# Revit family: 306_H7_W_-S7
name_source: partatom
category: Pipe Accessories
units: mm (PartAtom-declared; Revit-internal decimal feet)

## family parameters
Always vertical = Yes
Cut with Voids When Loaded = No
Part Type = Valve - Breaks Into
Round Connector Dimension = Use Diameter
Shared = No
Work Plane-Based = No

## types (2) — shared parameters
BH = 10 mm  [stored 0.0328084 ft]
BL = 150 mm  [stored 0.492126 ft]
CAT0 = Yes
Description = Globe valve, 3-way, Flange, PN 16
L2D_Min = 3048 mm
Manufacturer = Belimo
QmdConnectorList = 301;D;302;D;303;D
X1 = 100 mm  [stored 0.328084 ft]
magiPartTypeId = 306
magiProductFamilyId = H7*W*-S7
zero-valued in all types: MC_Default_elevation

## per-type parameters (varying)
| type | C | C__ve | D | DB | DM | DM2 | DM3 | DM4 | DT | FD | H | H12 | H2 | HM | HM1 | HM1__ve | HM2 | HM2__ve | HM__ve | L2 | L2D | LM | W2D |
| H7200W630-S7 | 30 mm  [stored 0.0984252 ft] | -30 mm  [stored -0.0984252 ft] | 200 mm | 250 mm  [stored 0.82021 ft] | 278 mm  [stored 0.912073 ft] | 200 mm  [stored 0.656168 ft] | 334 mm | 167 mm | 350 mm  [stored 1.14829 ft] | 340 mm  [stored 1.11549 ft] | 380 mm  [stored 1.24672 ft] | 110 mm  [stored 0.360892 ft] | 85 mm | 190 mm  [stored 0.62336 ft] | 95 mm  [stored 0.31168 ft] | -95 mm  [stored -0.31168 ft] | 65 mm  [stored 0.213255 ft] | -65 mm  [stored -0.213255 ft] | -190 mm  [stored -0.62336 ft] | 300 mm  [stored 0.984252 ft] | 600 mm | 540 mm | 200 mm  [stored 0.656168 ft] |
| H7250W1000-S7 | 32 mm  [stored 0.104987 ft] | -32 mm  [stored -0.104987 ft] | 250 mm | 313 mm | 344 mm  [stored 1.12861 ft] | 250 mm  [stored 0.82021 ft] | 413 mm | 206 mm | 438 mm | 405 mm  [stored 1.32874 ft] | 440 mm  [stored 1.44357 ft] | 131 mm | 103 mm | 220 mm  [stored 0.721785 ft] | 110 mm  [stored 0.360892 ft] | -110 mm  [stored -0.360892 ft] | 78 mm  [stored 0.255906 ft] | -78 mm  [stored -0.255906 ft] | -220 mm  [stored -0.721785 ft] | 365 mm  [stored 1.19751 ft] | 730 mm | 666 mm | 250 mm  [stored 0.82021 ft] |

note: column(s) folded — value = type name in every type: magiProductCode, magiProductId

note: [stored X ft] marks values corroborated as IEEE doubles in the binary element streams (Revit-internal decimal feet)

## geometry (parser evidence)
native form markers: Sweep x2
no freeform markers — native parametric forms only
